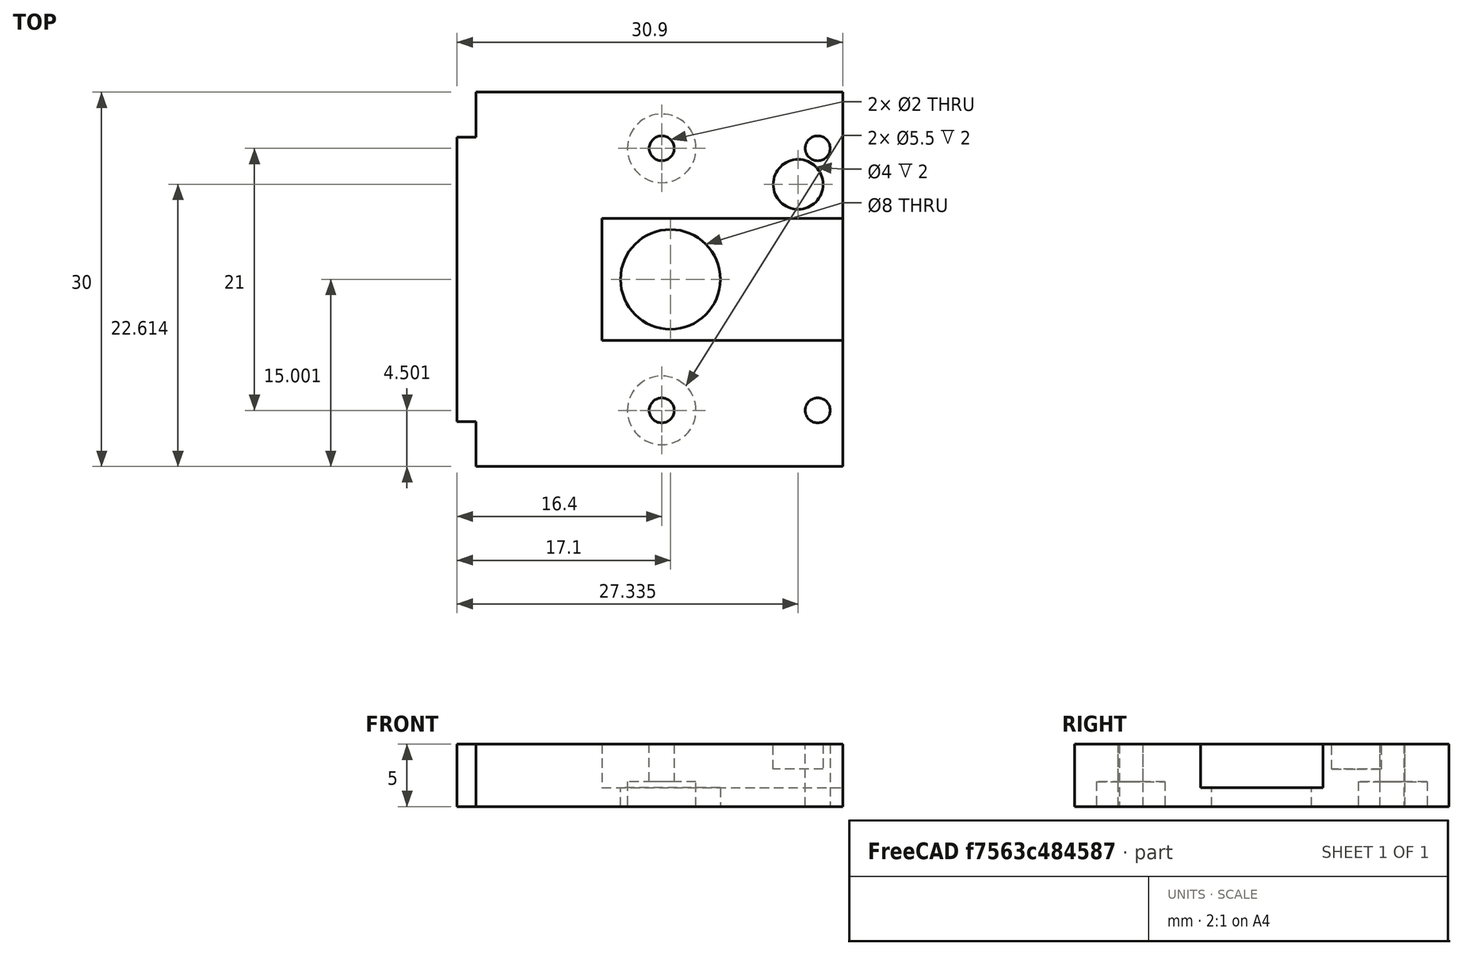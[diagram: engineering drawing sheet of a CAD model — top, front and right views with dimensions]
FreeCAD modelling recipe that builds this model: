
FCSTD DOCUMENT  (FreeCAD 0.18.3R)
Label: Lens.Cover
License: All rights reserved
LicenseURL: http://en.wikipedia.org/wiki/All_rights_reserved
objects: Part::Extrusion×11, Part::Part2DObjectPython×10, Part::Cut×7, Part::MultiFuse×1
note: 29 computed .brp shape members not serialized (recipe doc carries the construction recipe); baked Part::Feature solids carry a one-line shape summary decoded from their .brp

FEATURE [Part::Part2DObjectPython] Rectangle043  # Draft 2D object (typed FeaturePython)
  ChamferSize = 0
  Columns = 1
  FilletRadius = 0
  Height = 30
  Length = 29.4
  MakeFace = true
  Placement = pos=(12.6799,-119.849,-14.1) rot=(0,0,1;0rad)
  Rows = 1
FEATURE [Part::Part2DObjectPython] Rectangle044  # Draft 2D object (typed FeaturePython)
  ChamferSize = 0
  Columns = 1
  FilletRadius = 0
  Height = 22.8
  Length = 1.5
  MakeFace = true
  Placement = pos=(11.1799,-116.249,-14.1) rot=(0,0,1;0rad)
  Rows = 1
FEATURE [Part::Part2DObjectPython] Rectangle045  # Draft 2D object (typed FeaturePython)
  ChamferSize = 0
  Columns = 1
  FilletRadius = 0
  Height = 9.8
  Length = 19.3
  MakeFace = true
  Placement = pos=(22.7799,-109.749,-14.1) rot=(0,0,1;0rad)
  Rows = 1
FEATURE [Part::Part2DObjectPython] Circle022  # Draft 2D object (typed FeaturePython)
  FirstAngle = 0
  LastAngle = 0
  MakeFace = true
  Placement = pos=(28.2799,-104.849,-14.1) rot=(0,0,1;0rad)
  Radius = 4
FEATURE [Part::Part2DObjectPython] Circle025  # Draft 2D object (typed FeaturePython)
  FirstAngle = 0
  LastAngle = 0
  MakeFace = true
  Placement = pos=(27.5799,-115.349,-14.1) rot=(0,0,1;0rad)
  Radius = 1
FEATURE [Part::Extrusion] Extrude083
  Base = -> Rectangle043
  Dir = (0,0,1)
  DirMode = 2
  FaceMakerClass = Part::FaceMakerBullseye
  LengthFwd = -5
  LengthRev = 0
  Solid = false
  Symmetric = false
FEATURE [Part::Extrusion] Extrude085
  Base = -> Rectangle045
  Dir = (0,0,1)
  DirMode = 2
  FaceMakerClass = Part::FaceMakerBullseye
  LengthFwd = -3.5
  LengthRev = 0
  Solid = false
  Symmetric = false
FEATURE [Part::Cut] Cut027
  Base = -> Extrude083
  Tool = -> Extrude085
FEATURE [Part::Extrusion] Extrude088
  Base = -> Circle025
  Dir = (0,0,1)
  DirMode = 2
  FaceMakerClass = Part::FaceMakerBullseye
  LengthFwd = -5
  LengthRev = 0
  Solid = false
  Symmetric = false
FEATURE [Part::Extrusion] Extrude095
  Base = -> Rectangle044
  Dir = (0,0,1)
  DirMode = 2
  FaceMakerClass = Part::FaceMakerBullseye
  LengthFwd = -5
  LengthRev = 0
  Solid = false
  Symmetric = false
FEATURE [Part::Part2DObjectPython] Circle030  # Draft 2D object (typed FeaturePython)
  FirstAngle = 0
  LastAngle = 0
  MakeFace = true
  Placement = pos=(27.5799,-94.3491,-19.1) rot=(0,0,1;0rad)
  Radius = 2.75
FEATURE [Part::Part2DObjectPython] Circle031  # Draft 2D object (typed FeaturePython)
  FirstAngle = 0
  LastAngle = 0
  MakeFace = true
  Placement = pos=(27.5799,-115.349,-19.1) rot=(0,0,1;0rad)
  Radius = 2.75
FEATURE [Part::Extrusion] Extrude160
  Base = -> Circle022
  Dir = (0,0,1)
  DirMode = 2
  FaceMakerClass = Part::FaceMakerBullseye
  LengthFwd = -5
  LengthRev = 0
  Solid = false
  Symmetric = false
FEATURE [Part::Part2DObjectPython] Circle034  # Draft 2D object (typed FeaturePython)
  FirstAngle = 0
  LastAngle = 0
  MakeFace = true
  Placement = pos=(38.5147,-97.236,-14.1) rot=(0,0,1;0rad)
  Radius = 2
FEATURE [Part::Extrusion] Extrude206
  Base = -> Circle034
  Dir = (0,0,1)
  DirMode = 2
  FaceMakerClass = Part::FaceMakerBullseye
  LengthFwd = -2
  LengthRev = 0
  Solid = false
  Symmetric = false
FEATURE [Part::Part2DObjectPython] Circle023  # Draft 2D object (typed FeaturePython)
  FirstAngle = 0
  LastAngle = 0
  MakeFace = true
  Placement = pos=(40.0799,-94.3491,-14.1) rot=(0,0,1;0rad)
  Radius = 1
FEATURE [Part::Part2DObjectPython] Circle024  # Draft 2D object (typed FeaturePython)
  FirstAngle = 0
  LastAngle = 0
  MakeFace = true
  Placement = pos=(40.0799,-115.349,-14.1) rot=(0,0,1;0rad)
  Radius = 1
FEATURE [Part::Extrusion] Extrude087
  Base = -> Circle023
  Dir = (0,0,1)
  DirMode = 2
  FaceMakerClass = Part::FaceMakerBullseye
  LengthFwd = -5
  LengthRev = 0
  Solid = false
  Symmetric = false
FEATURE [Part::Extrusion] Extrude089
  Base = -> Circle024
  Dir = (0,0,1)
  DirMode = 2
  FaceMakerClass = Part::FaceMakerBullseye
  LengthFwd = -5
  LengthRev = 0
  Solid = false
  Symmetric = false
FEATURE [Part::Extrusion] Extrude086
  Dir = (0,0,1)
  DirMode = 2
  FaceMakerClass = Part::FaceMakerBullseye
  LengthFwd = -5
  LengthRev = 0
  Solid = false
  Symmetric = false
FEATURE [Part::Extrusion] Extrude
  Base = -> Circle030
  Dir = (0,0,1)
  DirMode = 2
  FaceMakerClass = Part::FaceMakerBullseye
  LengthFwd = 2
  LengthRev = 0
  Solid = false
  Symmetric = false
FEATURE [Part::Extrusion] Extrude207
  Base = -> Circle031
  Dir = (0,0,1)
  DirMode = 2
  FaceMakerClass = Part::FaceMakerBullseye
  LengthFwd = 2
  LengthRev = 0
  Solid = false
  Symmetric = false
FEATURE [Part::Cut] Cut
  Base = -> Cut027
  Tool = -> Extrude
FEATURE [Part::Cut] Cut028
  Base = -> Cut
  Tool = -> Extrude207
FEATURE [Part::Cut] Cut029
  Base = -> Cut028
  Tool = -> Extrude160
FEATURE [Part::Cut] Cut030
  Base = -> Cut029
  Tool = -> Extrude086
FEATURE [Part::Cut] Cut031
  Base = -> Cut030
  Tool = -> Extrude088
FEATURE [Part::Cut] Cut032
  Base = -> Cut031
  Tool = -> Extrude206
FEATURE [Part::MultiFuse] Fusion
  Shapes = -> [Cut032,Extrude095]
